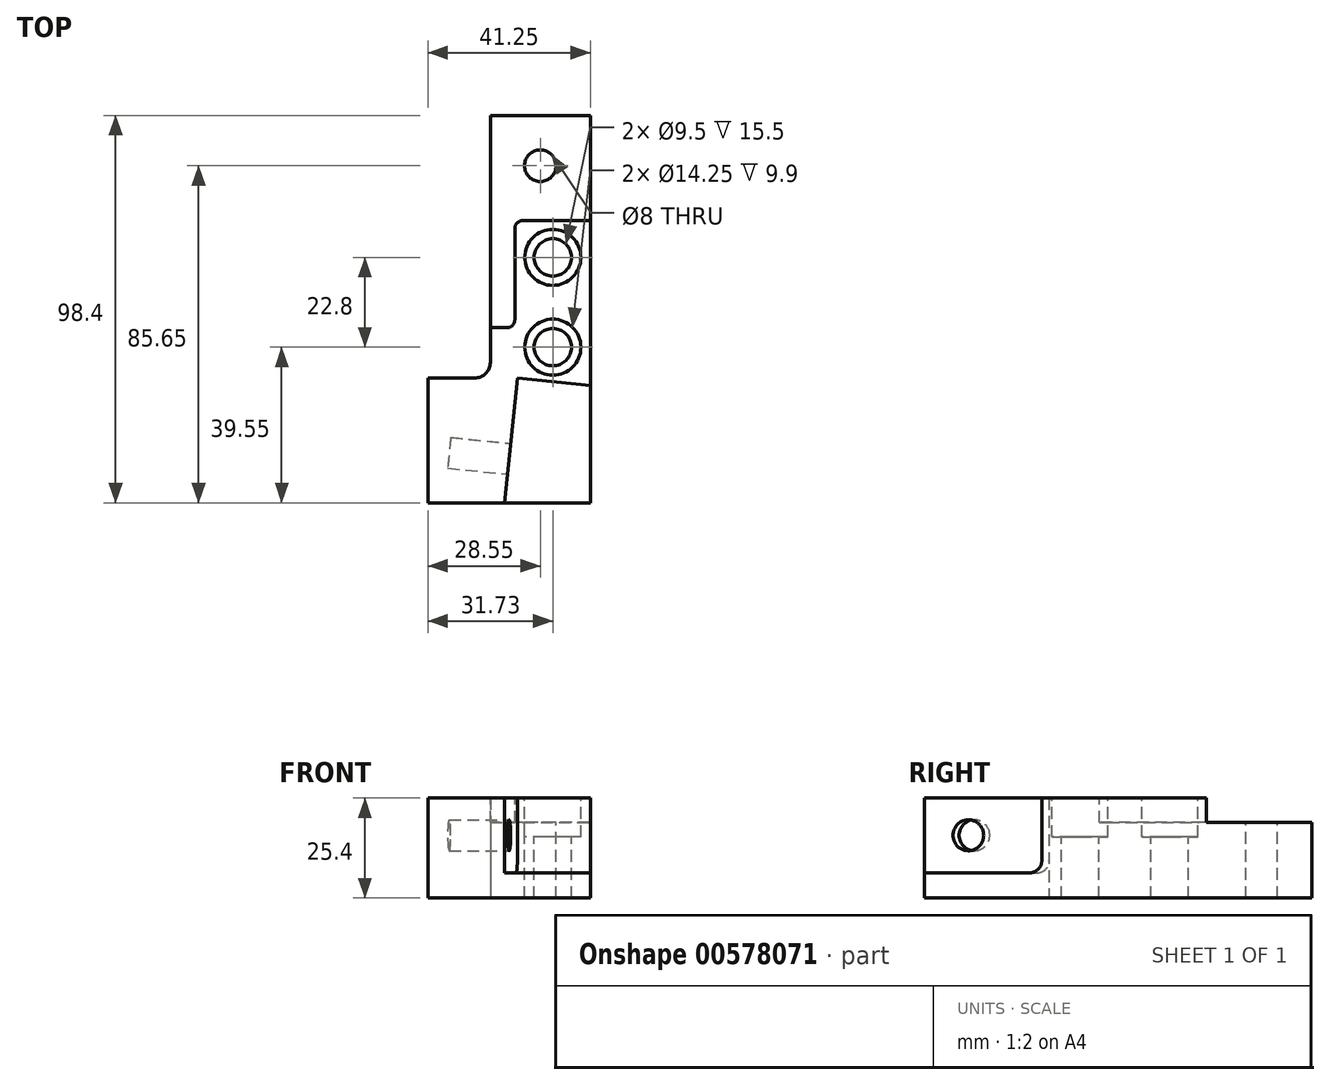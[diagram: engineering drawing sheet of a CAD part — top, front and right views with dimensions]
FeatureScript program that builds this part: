
annotation { "Feature Type Name" : "Feature", "Feature Type Description" : "" }
export const myFeature = defineFeature(function(context is Context, id is Id, definition is map)
    precondition{}
    {
        {
            var Q0;
            Q0=qCreatedBy(makeId("Top.planeOp"),FACE);
            var sketch = newSketch(context, id + "F0", { "sketchPlane" : qUnion([Q0])});
            skLineSegment(sketch, "E0", {"start": v(0, 49.2) * mm, "end": v(0, -49.2) * mm});
            skLineSegment(sketch, "E1", {"start": v(0, -49.2) * mm, "end": v(-41.25, -49.2) * mm});
            skLineSegment(sketch, "E2", {"start": v(-41.25, -49.2) * mm, "end": v(-41.25, -17.5) * mm});
            skLineSegment(sketch, "E3", {"start": v(0, 49.2) * mm, "end": v(-25.4, 49.2) * mm});
            skLineSegment(sketch, "E4", {"start": v(-25.4, 49.2) * mm, "end": v(-25.4, -13.5) * mm});
            skLineSegment(sketch, "E5", {"start": v(-29.4, -17.5) * mm, "end": v(-41.25, -17.5) * mm});
            skPoint(sketch, "E6.visualSharp", {"position": v(-25.4, -17.5) * mm});
            skArc(sketch, "E6.filletArc", {"start": v(-29.4, -17.5) * mm, "mid": v(-26.57, -16.33) * mm, "end": v(-25.4, -13.5) * mm});
            skSolve(sketch);
        }
        {
            var Q0;
            Q0=makeQuery(id+"F0.imprint","IMPRINT",FACE,{"disambiguationData":[TD([[makeQuery(id+"F0.imprint","IMPRINT",EDGE,{"derivedFrom":sQuery(id+"F0.wireOp",EDGE,"E0")}),-1.0]])]});
            extrude(context, id + "F1", {"entities" : qUnion([Q0]), "depth" : 25.4 * mm, "offsetDistance" : 25 * mm});
        }
        {
            var Q0;
            Q0=makeQuery(id+"F1.opExtrude","CAP_FACE",FACE,{"disambiguationData":[OSD([sQuery(id+"F0.wireOp",EDGE,"E0"),sQuery(id+"F0.wireOp",EDGE,"E1"),sQuery(id+"F0.wireOp",EDGE,"E2"),sQuery(id+"F0.wireOp",EDGE,"E3"),sQuery(id+"F0.wireOp",EDGE,"E4"),sQuery(id+"F0.wireOp",EDGE,"E5"),sQuery(id+"F0.wireOp",EDGE,"E6.filletArc")])],"isStart":false});
            var sketch = newSketch(context, id + "F2", { "sketchPlane" : qUnion([Q0])});
            skLineSegment(sketch, "E7", {"start": v(-25.4, 49.2) * mm, "end": v(-25.4, -4.7) * mm});
            skLineSegment(sketch, "E8", {"start": v(-25.4, -4.7) * mm, "end": v(-21.17, -4.7) * mm});
            skLineSegment(sketch, "E9", {"start": v(-19.17, -2.7) * mm, "end": v(-19.17, 20.5) * mm});
            skLineSegment(sketch, "E10", {"start": v(-17.17, 22.5) * mm, "end": v(0, 22.5) * mm});
            skLineSegment(sketch, "E11", {"start": v(0, 22.5) * mm, "end": v(0, 49.2) * mm});
            skLineSegment(sketch, "E12", {"start": v(0, 49.2) * mm, "end": v(-25.4, 49.2) * mm});
            skPoint(sketch, "E13.visualSharp", {"position": v(-19.17, 22.5) * mm});
            skArc(sketch, "E13.filletArc", {"start": v(-17.17, 22.5) * mm, "mid": v(-18.58, 21.91) * mm, "end": v(-19.17, 20.5) * mm});
            skPoint(sketch, "E14.visualSharp", {"position": v(-19.17, -4.7) * mm});
            skArc(sketch, "E14.filletArc", {"start": v(-21.17, -4.7) * mm, "mid": v(-19.76, -4.11) * mm, "end": v(-19.17, -2.7) * mm});
            skSolve(sketch);
        }
        {
            var Q0;
            Q0=makeQuery(id+"F2.imprint","IMPRINT",FACE,{"disambiguationData":[TD([[makeQuery(id+"F2.imprint","IMPRINT",EDGE,{"derivedFrom":sQuery(id+"F2.wireOp",EDGE,"E7")}),1.0]])]});
            extrude(context, id + "F3", {"entities" : qUnion([Q0]), "operationType" : NewBodyOperationType.REMOVE, "oppositeDirection" : true, "depth" : 6.22 * mm, "offsetDistance" : 25 * mm});
        }
        {
            var Q0;
            Q0=makeQuery(id+"F1.opExtrude","CAP_FACE",FACE,{"disambiguationData":[OSD([sQuery(id+"F0.wireOp",EDGE,"E0"),sQuery(id+"F0.wireOp",EDGE,"E1"),sQuery(id+"F0.wireOp",EDGE,"E2"),sQuery(id+"F0.wireOp",EDGE,"E3"),sQuery(id+"F0.wireOp",EDGE,"E4"),sQuery(id+"F0.wireOp",EDGE,"E5"),sQuery(id+"F0.wireOp",EDGE,"E6.filletArc")])],"isStart":false});
            var sketch = newSketch(context, id + "F4", { "sketchPlane" : qUnion([Q0])});
            skLineSegment(sketch, "E15", {"start": v(-41.25, -49.2) * mm, "end": v(-21.75, -49.2) * mm, "construction": true});
            skLineSegment(sketch, "E16", {"start": v(-41.25, -17.5) * mm, "end": v(-18.53, -17.5) * mm, "construction": true});
            skLineSegment(sketch, "E17", {"start": v(-21.75, -49.2) * mm, "end": v(-18.53, -17.5) * mm, "construction": true});
            skSolve(sketch);
        }
        {
            var Q0;
            Q0=sQuery(id+"F4.wireOp",EDGE,"E17");
            cPlane(context, id + "F5", {"entities" : qUnion([Q0]), "cplaneType" : CPlaneType.LINE_ANGLE, "offset" : 25 * mm, "angle" : 90 * degree, "width" : 150 * mm, "height" : 150 * mm});
        }
        {
            var Q0;
            Q0=qCreatedBy(id+"F5.planeOp",FACE);
            var sketch = newSketch(context, id + "F6", { "sketchPlane" : qUnion([Q0])});
            skLineSegment(sketch, "E18.0", {"start": v(-51.15, 25.4) * mm, "end": v(-19.28, 25.4) * mm, "construction": true});
            skLineSegment(sketch, "E19", {"start": v(-51.15, 25.4) * mm, "end": v(-56.15, 25.4) * mm, "construction": true});
            skLineSegment(sketch, "E20", {"start": v(-19.28, 25.4) * mm, "end": v(-19.28, 30.4) * mm, "construction": true});
            skLineSegment(sketch, "E21", {"start": v(-56.15, 25.4) * mm, "end": v(-56.15, 30.4) * mm, "construction": true});
            skLineSegment(sketch, "E22", {"start": v(-19.28, 30.4) * mm, "end": v(-56.15, 30.4) * mm});
            skLineSegment(sketch, "E23", {"start": v(-56.15, 30.4) * mm, "end": v(-56.15, 6.4) * mm});
            skPoint(sketch, "E23.endSnap0", {"position": v(-56.15, 27.9) * mm});
            skLineSegment(sketch, "E24", {"start": v(-19.28, 30.4) * mm, "end": v(-19.28, 9.4) * mm});
            skLineSegment(sketch, "E25", {"start": v(-56.15, 6.4) * mm, "end": v(-22.28, 6.4) * mm});
            skPoint(sketch, "E26.visualSharp", {"position": v(-19.28, 6.4) * mm});
            skArc(sketch, "E26.filletArc", {"start": v(-22.28, 6.4) * mm, "mid": v(-20.16, 7.28) * mm, "end": v(-19.28, 9.4) * mm});
            skSolve(sketch);
        }
        {
            var Q0;
            Q0=makeQuery(id+"F6.imprint","IMPRINT",FACE,{"disambiguationData":[TD([[makeQuery(id+"F6.imprint","IMPRINT",EDGE,{"derivedFrom":sQuery(id+"F6.wireOp",EDGE,"E22")}),1.0]])]});
            extrude(context, id + "F7", {"entities" : qUnion([Q0]), "operationType" : NewBodyOperationType.REMOVE, "depth" : 25 * mm, "offsetDistance" : 25 * mm});
        }
        {
            var Q0;
            Q0=qCreatedBy(id+"F5.planeOp",FACE);
            var sketch = newSketch(context, id + "F8", { "sketchPlane" : qUnion([Q0])});
            skCircle(sketch, "E27", {"center": v(-39.92, 15.93) * mm, "radius": 3.92 * mm});
            skLineSegment(sketch, "E28.0", {"start": v(-51.15, 25.4) * mm, "end": v(-19.28, 25.4) * mm, "construction": true});
            skLineSegment(sketch, "E29", {"start": v(-51.15, 25.4) * mm, "end": v(-51.15, 0) * mm, "construction": true});
            skLineSegment(sketch, "E30", {"start": v(-35.21, 25.4) * mm, "end": v(-35.21, 19.86) * mm, "construction": true});
            skLineSegment(sketch, "E31", {"start": v(-51.15, 12.7) * mm, "end": v(-43.85, 12.7) * mm, "construction": true});
            skLineSegment(sketch, "E32", {"start": v(-19.28, 19.86) * mm, "end": v(-51.15, 19.86) * mm, "construction": true});
            skLineSegment(sketch, "E33", {"start": v(-43.85, 25.4) * mm, "end": v(-43.85, 0) * mm, "construction": true});
            skSolve(sketch);
        }
        {
            var Q0;
            Q0=makeQuery(id+"F8.imprint","IMPRINT",FACE,{"disambiguationData":[TD([[makeQuery(id+"F8.imprint","IMPRINT",EDGE,{"derivedFrom":sQuery(id+"F8.wireOp",EDGE,"E27")}),1.0]])]});
            extrude(context, id + "F9", {"entities" : qUnion([Q0]), "operationType" : NewBodyOperationType.REMOVE, "oppositeDirection" : true, "depth" : 15.3 * mm, "offsetDistance" : 25 * mm});
        }
        {
            var Q0;
            Q0=makeQuery(id+"F3.boolean.opBoolean","COPY",FACE,{"derivedFrom":makeQuery(id+"F3.opExtrude","CAP_FACE",FACE,{"disambiguationData":[OSD([sQuery(id+"F2.wireOp",EDGE,"E7"),sQuery(id+"F2.wireOp",EDGE,"E8"),sQuery(id+"F2.wireOp",EDGE,"E9"),sQuery(id+"F2.wireOp",EDGE,"E10"),sQuery(id+"F2.wireOp",EDGE,"E11"),sQuery(id+"F2.wireOp",EDGE,"E12"),sQuery(id+"F2.wireOp",EDGE,"E13.filletArc"),sQuery(id+"F2.wireOp",EDGE,"E14.filletArc")])],"isStart":false})});
            var sketch = newSketch(context, id + "F10", { "sketchPlane" : qUnion([Q0])});
            skCircle(sketch, "E34", {"center": v(-12.7, 36.45) * mm, "radius": 4 * mm});
            skLineSegment(sketch, "E35", {"start": v(-12.7, 49.2) * mm, "end": v(-12.7, 40.45) * mm, "construction": true});
            skLineSegment(sketch, "E36", {"start": v(-25.4, 40.45) * mm, "end": v(0, 40.45) * mm, "construction": true});
            skLineSegment(sketch, "E37", {"start": v(-12.7, 36.45) * mm, "end": v(-12.7, 49.2) * mm, "construction": true});
            skSolve(sketch);
        }
        {
            var Q0;
            Q0=makeQuery(id+"F10.imprint","IMPRINT",FACE,{"disambiguationData":[TD([[makeQuery(id+"F10.imprint","IMPRINT",EDGE,{"derivedFrom":sQuery(id+"F10.wireOp",EDGE,"E34")}),1.0]])]});
            var Q1;
            Q1=sQuery(id+"F10.wireOp",EDGE,"E34");
            extrude(context, id + "F11", {"entities" : qUnion([Q0]), "operationType" : NewBodyOperationType.REMOVE, "surfaceEntities" : qUnion([Q1]), "endBound" : BoundingType.THROUGH_ALL, "oppositeDirection" : true, "depth" : 25 * mm, "offsetDistance" : 25 * mm});
        }
        {
            var Q0;
            Q0=makeQuery(id+"F4.imprint","IMPRINT",FACE,{"disambiguationData":[TD([[makeQuery(id+"F4.imprint","IMPRINT",EDGE,{"derivedFrom":makeQuery(id+"F1.opExtrude","CAP_EDGE",EDGE,{"disambiguationData":[OSD([sQuery(id+"F0.wireOp",EDGE,"E1")])],"isStart":false})}),-1.0]])]});
            var sketch = newSketch(context, id + "F12", { "sketchPlane" : qUnion([Q0])});
            skCircle(sketch, "E38", {"center": v(-9.52, 13.15) * mm, "radius": 4.75 * mm});
            skCircle(sketch, "E39", {"center": v(-9.52, -9.65) * mm, "radius": 4.75 * mm});
            skLineSegment(sketch, "E40", {"start": v(0, 1.56) * mm, "end": v(-4.77, 1.56) * mm, "construction": true});
            skLineSegment(sketch, "E41", {"start": v(-4.77, 21.56) * mm, "end": v(-4.77, -18.44) * mm, "construction": true});
            skLineSegment(sketch, "E42.0", {"start": v(0, -19.38) * mm, "end": v(-18.53, -17.5) * mm, "construction": true});
            skLineSegment(sketch, "E43.0", {"start": v(-17.17, 22.5) * mm, "end": v(0, 22.5) * mm, "construction": true});
            skLineSegment(sketch, "E44", {"start": v(-9.52, 22.5) * mm, "end": v(-9.52, 17.9) * mm, "construction": true});
            skLineSegment(sketch, "E45", {"start": v(-9.52, -4.9) * mm, "end": v(-9.52, 8.4) * mm, "construction": true});
            skSolve(sketch);
        }
        {
            var Q0;
            Q0=makeQuery(id+"F12.imprint","IMPRINT",FACE,{"disambiguationData":[TD([[makeQuery(id+"F12.imprint","IMPRINT",EDGE,{"derivedFrom":sQuery(id+"F12.wireOp",EDGE,"E38")}),1.0]])]});
            extrude(context, id + "F13", {"entities" : qUnion([Q0]), "operationType" : NewBodyOperationType.REMOVE, "endBound" : BoundingType.THROUGH_ALL, "oppositeDirection" : true, "depth" : 25 * mm, "offsetDistance" : 25 * mm});
        }
        {
            var Q0;
            Q0=makeQuery(id+"F12.imprint","IMPRINT",FACE,{"disambiguationData":[TD([[makeQuery(id+"F12.imprint","IMPRINT",EDGE,{"derivedFrom":sQuery(id+"F12.wireOp",EDGE,"E39")}),1.0]])]});
            extrude(context, id + "F14", {"entities" : qUnion([Q0]), "operationType" : NewBodyOperationType.REMOVE, "endBound" : BoundingType.THROUGH_ALL, "oppositeDirection" : true, "depth" : 25 * mm, "offsetDistance" : 25 * mm});
        }
        {
            var Q0;
            Q0=makeQuery(id+"F4.imprint","IMPRINT",FACE,{"disambiguationData":[TD([[makeQuery(id+"F4.imprint","IMPRINT",EDGE,{"derivedFrom":makeQuery(id+"F1.opExtrude","CAP_EDGE",EDGE,{"disambiguationData":[OSD([sQuery(id+"F0.wireOp",EDGE,"E1")])],"isStart":false})}),-1.0]])]});
            var sketch = newSketch(context, id + "F15", { "sketchPlane" : qUnion([Q0])});
            skCircle(sketch, "E46", {"center": v(-9.52, 13.15) * mm, "radius": 7.12 * mm});
            skCircle(sketch, "E47", {"center": v(-9.52, -9.65) * mm, "radius": 7.12 * mm});
            skSolve(sketch);
        }
        {
            var Q0;
            Q0=makeQuery(id+"F15.imprint","IMPRINT",FACE,{"disambiguationData":[TD([[makeQuery(id+"F15.imprint","IMPRINT",EDGE,{"derivedFrom":sQuery(id+"F15.wireOp",EDGE,"E46")}),1.0]])]});
            extrude(context, id + "F16", {"entities" : qUnion([Q0]), "operationType" : NewBodyOperationType.REMOVE, "oppositeDirection" : true, "depth" : 9.9 * mm, "offsetDistance" : 25 * mm});
        }
        {
            var Q0;
            Q0=makeQuery(id+"F15.imprint","IMPRINT",FACE,{"disambiguationData":[TD([[makeQuery(id+"F15.imprint","IMPRINT",EDGE,{"derivedFrom":sQuery(id+"F15.wireOp",EDGE,"E47")}),1.0]])]});
            extrude(context, id + "F17", {"entities" : qUnion([Q0]), "operationType" : NewBodyOperationType.REMOVE, "oppositeDirection" : true, "depth" : 9.9 * mm, "offsetDistance" : 25 * mm});
        }
    });
